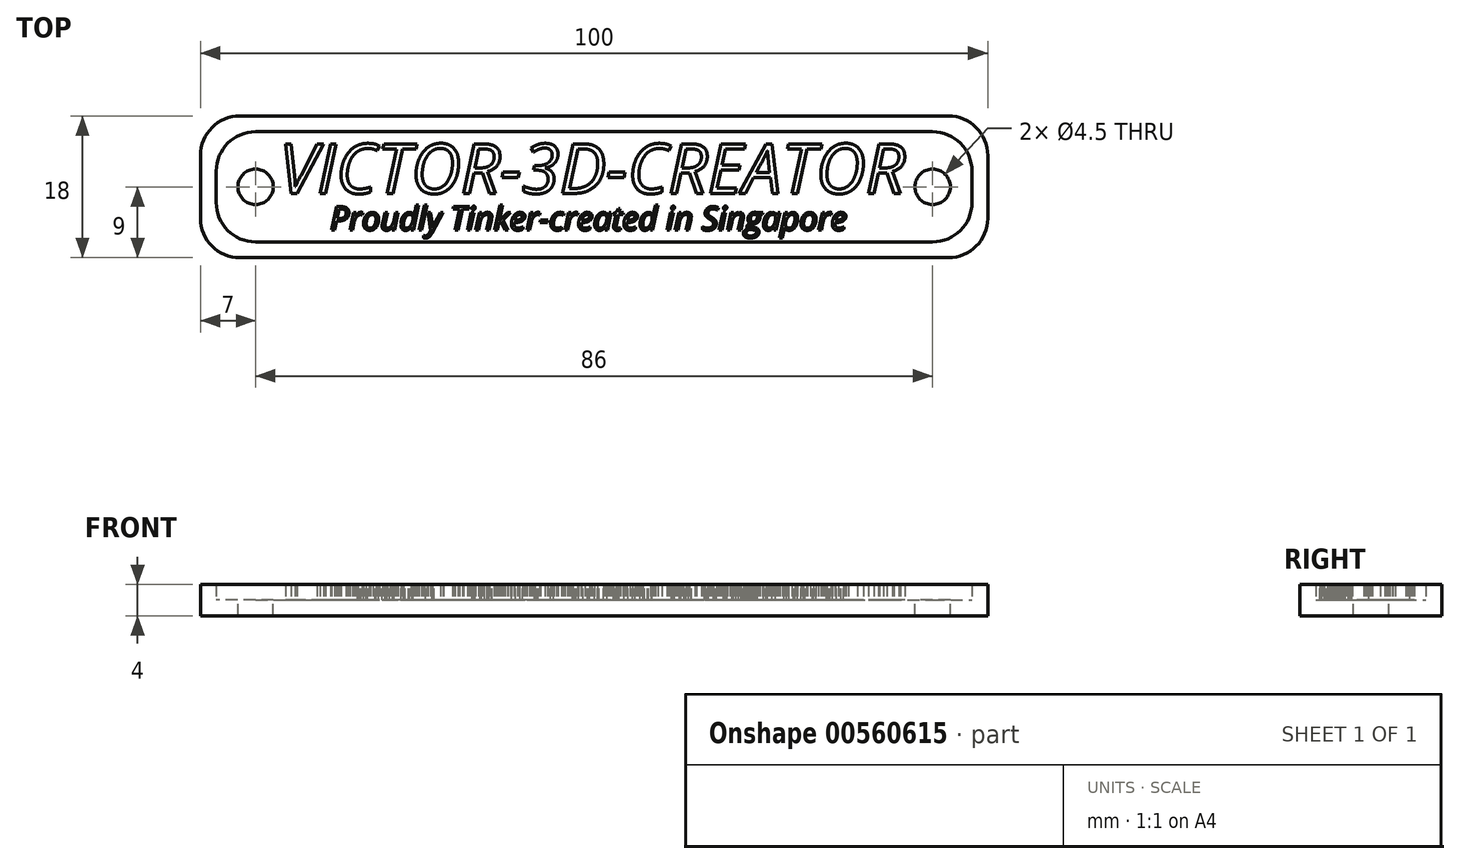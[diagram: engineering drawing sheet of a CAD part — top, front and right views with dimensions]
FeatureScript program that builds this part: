
annotation { "Feature Type Name" : "Feature", "Feature Type Description" : "" }
export const myFeature = defineFeature(function(context is Context, id is Id, definition is map)
    precondition{}
    {
        {
            var Q0;
            Q0=qCreatedBy(makeId("Top.planeOp"),FACE);
            var sketch = newSketch(context, id + "F0", { "sketchPlane" : qUnion([Q0])});
            skLineSegment(sketch, "E0.bottom", {"start": v(0, 0) * mm, "end": v(100, 0) * mm});
            skLineSegment(sketch, "E0.top", {"start": v(0, 18) * mm, "end": v(100, 18) * mm});
            skLineSegment(sketch, "E0.left", {"start": v(0, 0) * mm, "end": v(0, 18) * mm});
            skLineSegment(sketch, "E0.right", {"start": v(100, 0) * mm, "end": v(100, 18) * mm});
            skCircle(sketch, "E1", {"center": v(7, 9) * mm, "radius": 2.25 * mm});
            skCircle(sketch, "E2", {"center": v(93, 9) * mm, "radius": 2.25 * mm});
            skSolve(sketch);
        }
        {
            var Q0;
            Q0 = qSketchRegion(id + "F0", true);
            extrude(context, id + "F1", {"entities" : qUnion([Q0]), "oppositeDirection" : true, "depth" : 2 * mm, "offsetDistance" : 25 * mm});
        }
        {
            var Q0;
            Q0=makeQuery(id+"F1.opExtrude","CAP_FACE",FACE,{"disambiguationData":[OSD([sQuery(id+"F0.wireOp",EDGE,"E0.bottom"),sQuery(id+"F0.wireOp",EDGE,"E0.top"),sQuery(id+"F0.wireOp",EDGE,"E0.left"),sQuery(id+"F0.wireOp",EDGE,"E0.right"),sQuery(id+"F0.wireOp",EDGE,"E1"),sQuery(id+"F0.wireOp",EDGE,"E2")])],"isStart":true});
            var sketch = newSketch(context, id + "F2", { "sketchPlane" : qUnion([Q0])});
            skText(sketch, "E3", { "text": "VICTOR-3D-CREATOR", "fontName": "OpenSans-Italic.ttf"});
            const initialGuessF2  = {"E3": [0.01, 0.00817, 1, 0, 0.00633]};
            skSetInitialGuess(sketch, initialGuessF2);
            skSolve(sketch);
        }
        {
            var Q0;
            Q0 = qSketchRegion(id + "F2", true);
            extrude(context, id + "F3", {"entities" : qUnion([Q0]), "operationType" : NewBodyOperationType.ADD, "depth" : 2 * mm, "offsetDistance" : 25 * mm});
        }
        {
            var Q0;
            {var subQ0=sQuery(id+"F0.wireOp",EDGE,"E0.top");var subQ118=sQuery(id+"F0.wireOp",EDGE,"E0.right");var subQ127=sQuery(id+"F0.wireOp",EDGE,"E0.bottom");var subQ128=makeQuery(id+"F1.opExtrude","SWEPT_FACE",FACE,{"disambiguationData":[OSD([subQ127])]});var subQ129=sQuery(id+"F0.wireOp",EDGE,"E1");var subQ139=sQuery(id+"F0.wireOp",EDGE,"E2");var subQ143=sQuery(id+"F0.wireOp",EDGE,"E0.left");Q0=makeQuery(id+"FFJBjQclBaa1cPK_1.boolean.opBoolean","SPLIT",FACE,{"disambiguationData":[TD([subQ128])],"derivedFrom":makeQuery(id+"F3.boolean.opBoolean","SPLIT",FACE,{"disambiguationData":[TD([subQ128])],"derivedFrom":makeQuery(id+"F1.opExtrude","CAP_FACE",FACE,{"disambiguationData":[OSD([subQ127,subQ0,subQ143,subQ118,subQ129,subQ139])],"isStart":true})})});}
            var sketch = newSketch(context, id + "F4", { "sketchPlane" : qUnion([Q0])});
            skLineSegment(sketch, "E4.bottom", {"start": v(2, 16) * mm, "end": v(98, 16) * mm});
            skLineSegment(sketch, "E4.top", {"start": v(2, 2) * mm, "end": v(98, 2) * mm});
            skLineSegment(sketch, "E4.left", {"start": v(2, 16) * mm, "end": v(2, 2) * mm});
            skLineSegment(sketch, "E4.right", {"start": v(98, 16) * mm, "end": v(98, 2) * mm});
            skSolve(sketch);
        }
        {
            var Q0;
            Q0=makeQuery(id+"F4.imprint","IMPRINT",FACE,{"disambiguationData":[TD([[makeQuery(id+"F4.imprint","IMPRINT",EDGE,{"derivedFrom":sQuery(id+"F4.wireOp",EDGE,"E4.bottom")}),1.0]])]});
            extrude(context, id + "F5", {"entities" : qUnion([Q0]), "operationType" : NewBodyOperationType.ADD, "depth" : 2 * mm, "offsetDistance" : 25 * mm});
        }
        {
            var Q0;
            {var subQ0=sQuery(id+"F0.wireOp",EDGE,"E0.left");var subQ1=sQuery(id+"F0.wireOp",EDGE,"E0.top");Q0=makeQuery(id+"F5.boolean.opBoolean","MERGE",EDGE,{"derivedFrom":[makeQuery(id+"F1.opExtrude","SWEPT_EDGE",EDGE,{"disambiguationData":[OSD([subQ1,subQ0])]}),makeQuery(id+"F5.opExtrude","SWEPT_EDGE",EDGE,{"disambiguationData":[OSD([subQ1,subQ0])]})]});}
            var Q1;
            {var subQ0=sQuery(id+"F0.wireOp",EDGE,"E0.left");var subQ1=sQuery(id+"F0.wireOp",EDGE,"E0.bottom");Q1=makeQuery(id+"F5.boolean.opBoolean","MERGE",EDGE,{"derivedFrom":[makeQuery(id+"F1.opExtrude","SWEPT_EDGE",EDGE,{"disambiguationData":[OSD([subQ1,subQ0])]}),makeQuery(id+"F5.opExtrude","SWEPT_EDGE",EDGE,{"disambiguationData":[OSD([subQ1,subQ0])]})]});}
            var Q2;
            {var subQ0=sQuery(id+"F0.wireOp",EDGE,"E0.right");var subQ1=sQuery(id+"F0.wireOp",EDGE,"E0.top");Q2=makeQuery(id+"F5.boolean.opBoolean","MERGE",EDGE,{"derivedFrom":[makeQuery(id+"F1.opExtrude","SWEPT_EDGE",EDGE,{"disambiguationData":[OSD([subQ1,subQ0])]}),makeQuery(id+"F5.opExtrude","SWEPT_EDGE",EDGE,{"disambiguationData":[OSD([subQ1,subQ0])]})]});}
            var Q3;
            {var subQ0=sQuery(id+"F0.wireOp",EDGE,"E0.right");var subQ1=sQuery(id+"F0.wireOp",EDGE,"E0.bottom");Q3=makeQuery(id+"F5.boolean.opBoolean","MERGE",EDGE,{"derivedFrom":[makeQuery(id+"F1.opExtrude","SWEPT_EDGE",EDGE,{"disambiguationData":[OSD([subQ1,subQ0])]}),makeQuery(id+"F5.opExtrude","SWEPT_EDGE",EDGE,{"disambiguationData":[OSD([subQ1,subQ0])]})]});}
            var Q4;
            Q4=makeQuery(id+"F5.opExtrude","SWEPT_EDGE",EDGE,{"disambiguationData":[OSD([sQuery(id+"F4.wireOp",EDGE,"E4.bottom"),sQuery(id+"F4.wireOp",EDGE,"E4.left")])]});
            var Q5;
            Q5=makeQuery(id+"F5.opExtrude","SWEPT_EDGE",EDGE,{"disambiguationData":[OSD([sQuery(id+"F4.wireOp",EDGE,"E4.top"),sQuery(id+"F4.wireOp",EDGE,"E4.left")])]});
            var Q6;
            Q6=makeQuery(id+"F5.opExtrude","SWEPT_EDGE",EDGE,{"disambiguationData":[OSD([sQuery(id+"F4.wireOp",EDGE,"E4.bottom"),sQuery(id+"F4.wireOp",EDGE,"E4.right")])]});
            var Q7;
            Q7=makeQuery(id+"F5.opExtrude","SWEPT_EDGE",EDGE,{"disambiguationData":[OSD([sQuery(id+"F4.wireOp",EDGE,"E4.top"),sQuery(id+"F4.wireOp",EDGE,"E4.right")])]});
            fillet(context, id + "F6", {"entities" : qUnion([Q0, Q1, Q2, Q3, Q4, Q5, Q6, Q7]), "radius" : 5 * mm, "tangentPropagation" : true, "allowEdgeOverflow" : false});
        }
        {
            var Q0;
            {var subQ0=sQuery(id+"F0.wireOp",EDGE,"E0.top");var subQ1=sQuery(id+"F0.wireOp",EDGE,"E0.right");var subQ2=sQuery(id+"F0.wireOp",EDGE,"E0.bottom");var subQ3=sQuery(id+"F0.wireOp",EDGE,"E1");var subQ4=sQuery(id+"F0.wireOp",EDGE,"E2");var subQ5=sQuery(id+"F0.wireOp",EDGE,"E0.left");Q0=makeQuery(id+"F3.boolean.opBoolean","SPLIT",FACE,{"disambiguationData":[TD([makeQuery(id+"F1.opExtrude","SWEPT_FACE",FACE,{"disambiguationData":[OSD([subQ2])]})])],"derivedFrom":makeQuery(id+"F1.opExtrude","CAP_FACE",FACE,{"disambiguationData":[OSD([subQ2,subQ0,subQ5,subQ1,subQ3,subQ4])],"isStart":true})});}
            var sketch = newSketch(context, id + "F7", { "sketchPlane" : qUnion([Q0])});
            skText(sketch, "E5", { "text": "Proudly Tinker-created in Singapore", "fontName": "OpenSans-Italic.ttf"});
            const initialGuessF7  = {"E5": [0.0165, 0.0035, 1, 0, 0.003]};
            skSetInitialGuess(sketch, initialGuessF7);
            skSolve(sketch);
        }
        {
            var Q0;
            Q0 = qSketchRegion(id + "F7", true);
            extrude(context, id + "F8", {"entities" : qUnion([Q0]), "operationType" : NewBodyOperationType.ADD, "depth" : 2 * mm, "offsetDistance" : 25 * mm});
        }
    });
